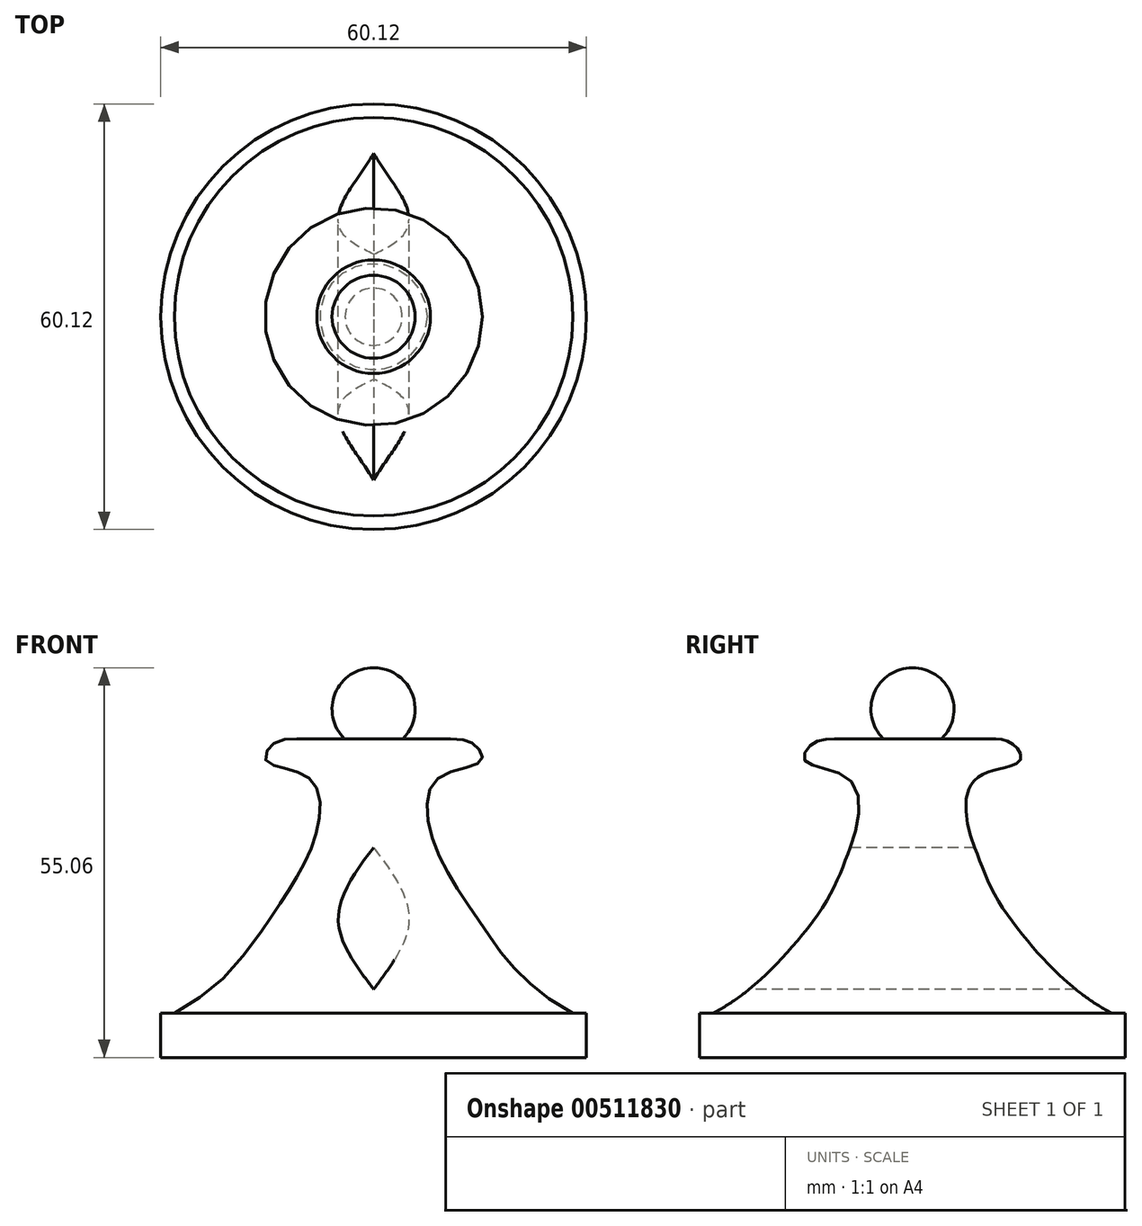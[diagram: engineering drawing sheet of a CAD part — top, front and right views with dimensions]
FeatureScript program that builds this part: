
annotation { "Feature Type Name" : "Feature", "Feature Type Description" : "" }
export const myFeature = defineFeature(function(context is Context, id is Id, definition is map)
    precondition{}
    {
        {
            var Q0;
            Q0=qCreatedBy(makeId("Front.planeOp"),FACE);
            var sketch = newSketch(context, id + "F0", { "sketchPlane" : qUnion([Q0])});
            skLineSegment(sketch, "E0", {"start": v(0, 0) * mm, "end": v(30.06, 0) * mm});
            skLineSegment(sketch, "E1", {"start": v(30.06, 0) * mm, "end": v(30.06, 6.25) * mm});
            skLineSegment(sketch, "E2", {"start": v(30.06, 6.25) * mm, "end": v(28.15, 6.25) * mm});
            skFitSpline(sketch, "E3", {"points": [v(28.15, 6.25) * mm, v(15, 19.13) * mm, v(8.4, 30.7) * mm, v(9.06, 39.41) * mm, v(15.2, 41.92) * mm, v(14.29, 44.19) * mm, v(8.02, 44.93) * mm], "startDerivative": vector(-89.57, 48.78) * mm, "endDerivative": vector(-70.34, -3.26) * mm});
            skLineSegment(sketch, "E4", {"start": v(8.02, 44.93) * mm, "end": v(4.03, 44.93) * mm});
            skArc(sketch, "E5", {"start": v(4.03, 44.93) * mm, "mid": v(5.45, 51.36) * mm, "end": v(0, 55.06) * mm});
            skLineSegment(sketch, "E6", {"start": v(0, 55.06) * mm, "end": v(0, 0) * mm});
            skPoint(sketch, "E7.orphan", {"position": v(0, 44.93) * mm});
            skSolve(sketch);
        }
        {
            var Q0;
            Q0 = qSketchRegion(id + "F0", true);
            var Q1;
            Q1=sQuery(id+"F0.wireOp",EDGE,"E6");
            revolve(context, id + "F1", {"entities" : qUnion([Q0]), "axis" : qUnion([Q1]), "revolveType" : RevolveType.FULL});
        }
        {
            var Q0;
            Q0=qCreatedBy(makeId("Front.planeOp"),FACE);
            var sketch = newSketch(context, id + "F2", { "sketchPlane" : qUnion([Q0])});
            skFitSpline(sketch, "E8", {"points": [v(0, 29.62) * mm, v(5, 19.62) * mm, v(0, 9.62) * mm], "startDerivative": vector(15.04, -19.4) * mm, "endDerivative": vector(-14.96, -20.1) * mm});
            skFitSpline(sketch, "E9.MirrorCS", {"points": [v(0, 29.62) * mm, v(-5, 19.62) * mm, v(0, 9.62) * mm], "startDerivative": vector(-15.04, -19.4) * mm, "endDerivative": vector(14.96, -20.1) * mm});
            skLineSegment(sketch, "E10", {"start": v(0, 29.62) * mm, "end": v(0, 9.62) * mm});
            skSolve(sketch);
        }
        {
            var Q0;
            Q0 = qSketchRegion(id + "F2", true);
            extrude(context, id + "F3", {"entities" : qUnion([Q0]), "operationType" : NewBodyOperationType.REMOVE, "endBound" : BoundingType.THROUGH_ALL, "oppositeDirection" : true, "depth" : 25 * mm, "offsetDistance" : 25 * mm, "hasSecondDirection" : true, "secondDirectionBound" : SecondDirectionBoundingType.THROUGH_ALL, "secondDirectionOppositeDirection" : false, "secondDirectionDepth" : 25 * mm});
        }
    });
